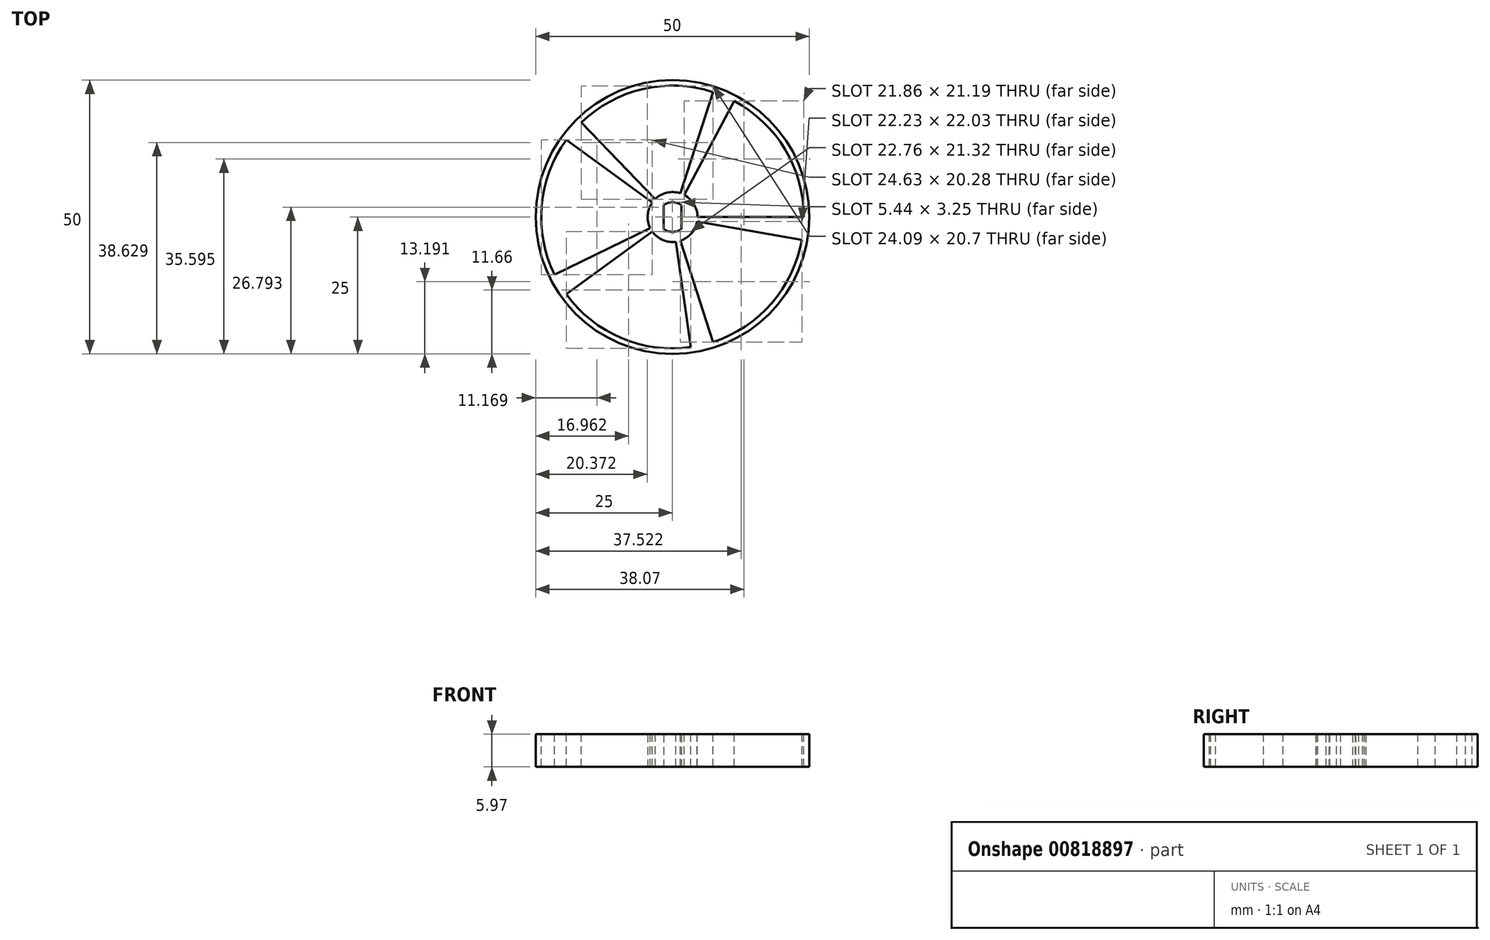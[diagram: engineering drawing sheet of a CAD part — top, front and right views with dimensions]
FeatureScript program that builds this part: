
annotation { "Feature Type Name" : "Feature", "Feature Type Description" : "" }
export const myFeature = defineFeature(function(context is Context, id is Id, definition is map)
    precondition{}
    {
        {
            var Q0;
            Q0=qCreatedBy(makeId("Top.planeOp"),FACE);
            var sketch = newSketch(context, id + "F0", { "sketchPlane" : qUnion([Q0])});
            skArc(sketch, "E0", {"start": v(2.6, 5.8) * mm, "mid": v(-6.35, 0) * mm, "end": v(2.6, -5.8) * mm});
            skLineSegment(sketch, "E1", {"start": v(2.6, 5.8) * mm, "end": v(15.56, 0) * mm});
            skLineSegment(sketch, "E2", {"start": v(15.56, 0) * mm, "end": v(2.6, -5.8) * mm});
            skCircle(sketch, "E3", {"center": v(0, 0) * mm, "radius": 4.56 * mm});
            skLineSegment(sketch, "E4.bottom", {"start": v(-1.63, 2.18) * mm, "end": v(1.63, 2.18) * mm, "construction": true});
            skLineSegment(sketch, "E4.top", {"start": v(-1.63, -2.18) * mm, "end": v(1.63, -2.18) * mm, "construction": true});
            skLineSegment(sketch, "E4.left", {"start": v(-1.63, 2.18) * mm, "end": v(-1.63, -2.18) * mm});
            skLineSegment(sketch, "E4.right", {"start": v(1.63, 2.18) * mm, "end": v(1.63, -2.18) * mm});
            skArc(sketch, "E5", {"start": v(1.63, 2.18) * mm, "mid": v(0, 2.72) * mm, "end": v(-1.63, 2.18) * mm});
            skArc(sketch, "E6", {"start": v(-1.63, -2.18) * mm, "mid": v(0, -2.72) * mm, "end": v(1.63, -2.18) * mm});
            skArc(sketch, "E7", {"start": v(5.5, -2.76) * mm, "mid": v(6.15, 0) * mm, "end": v(5.5, 2.76) * mm});
            skLineSegment(sketch, "E8", {"start": v(5.5, -2.76) * mm, "end": v(11.67, 0) * mm});
            skLineSegment(sketch, "E9", {"start": v(11.67, 0) * mm, "end": v(5.5, 2.76) * mm});
            skLineSegment(sketch, "E10", {"start": v(5.5, 2.76) * mm, "end": v(5.5, -2.76) * mm, "construction": true});
            skSolve(sketch);
        }
        {
            var Q0;
            Q0=makeQuery(id+"F0.imprint","IMPRINT",FACE,{"disambiguationData":[TD([[makeQuery(id+"F0.imprint","IMPRINT",EDGE,{"derivedFrom":sQuery(id+"F0.wireOp",EDGE,"E3")}),1.0]])]});
            extrude(context, id + "F1", {"entities" : qUnion([Q0]), "depth" : 5.97 * mm, "offsetDistance" : 25.4 * mm});
        }
        {
            var Q0;
            Q0=makeQuery(id+"F1.opExtrude","CAP_FACE",FACE,{"disambiguationData":[OSD([sQuery(id+"F0.wireOp",EDGE,"E3"),sQuery(id+"F0.wireOp",EDGE,"E4.left"),sQuery(id+"F0.wireOp",EDGE,"E4.right"),sQuery(id+"F0.wireOp",EDGE,"E5"),sQuery(id+"F0.wireOp",EDGE,"E6")])],"isStart":false});
            var sketch = newSketch(context, id + "F2", { "sketchPlane" : qUnion([Q0])});
            skCircle(sketch, "E11", {"center": v(0, 0) * mm, "radius": 25 * mm});
            skLineSegment(sketch, "E12", {"start": v(0, 0) * mm, "end": v(4.56, 0) * mm, "construction": true});
            skLineSegment(sketch, "E13", {"start": v(0, 0) * mm, "end": v(4.5, -0.8) * mm, "construction": true});
            skLineSegment(sketch, "E14", {"start": v(4.5, -0.8) * mm, "end": v(23.64, -4.17) * mm});
            skLineSegment(sketch, "E15", {"start": v(4.56, 0) * mm, "end": v(24, 0) * mm});
            skArc(sketch, "E16.0", {"start": v(4.5, -0.8) * mm, "mid": v(4.54, -0.4) * mm, "end": v(4.56, 0) * mm});
            skLineSegment(sketch, "E17.1.0", {"start": v(2.14, 4.03) * mm, "end": v(11.27, 21.2) * mm});
            skLineSegment(sketch, "E17.1.1", {"start": v(1.4, 4.34) * mm, "end": v(7.42, 22.83) * mm});
            skLineSegment(sketch, "E17.2.0", {"start": v(-3.17, 3.28) * mm, "end": v(-16.67, 17.26) * mm});
            skLineSegment(sketch, "E17.2.1", {"start": v(-3.69, 2.68) * mm, "end": v(-19.42, 14.1) * mm});
            skLineSegment(sketch, "E17.3.0", {"start": v(-4.1, -2) * mm, "end": v(-21.57, -10.52) * mm});
            skLineSegment(sketch, "E17.3.1", {"start": v(-3.69, -2.68) * mm, "end": v(-19.42, -14.1) * mm});
            skLineSegment(sketch, "E17.4.0", {"start": v(0.63, -4.51) * mm, "end": v(3.34, -23.77) * mm});
            skLineSegment(sketch, "E17.4.1", {"start": v(1.4, -4.34) * mm, "end": v(7.42, -22.83) * mm});
            skArc(sketch, "E18.trimOffspring", {"start": v(0.63, -4.51) * mm, "mid": v(1.03, -4.44) * mm, "end": v(1.4, -4.34) * mm});
            skArc(sketch, "E19.trimOffspring", {"start": v(-4.1, -2) * mm, "mid": v(-3.9, -2.35) * mm, "end": v(-3.69, -2.68) * mm});
            skArc(sketch, "E20.trimOffspring", {"start": v(-3.17, 3.28) * mm, "mid": v(-3.44, 3) * mm, "end": v(-3.69, 2.68) * mm});
            skArc(sketch, "E21.trimOffspring", {"start": v(2.14, 4.03) * mm, "mid": v(1.78, 4.2) * mm, "end": v(1.4, 4.34) * mm});
            skArc(sketch, "E22.0", {"start": v(24, 0) * mm, "mid": v(20.57, 12.36) * mm, "end": v(11.27, 21.2) * mm});
            skPoint(sketch, "E23.orphan", {"position": v(24.62, -4.34) * mm});
            skPoint(sketch, "E24.orphan", {"position": v(25, 0) * mm});
            skPoint(sketch, "E25.orphan", {"position": v(11.74, 22.07) * mm});
            skArc(sketch, "E26.trimOffspring", {"start": v(7.42, 22.83) * mm, "mid": v(-5.4, 23.38) * mm, "end": v(-16.67, 17.26) * mm});
            skPoint(sketch, "E27.orphan", {"position": v(7.73, 23.78) * mm});
            skArc(sketch, "E28.trimOffspring", {"start": v(-19.42, 14.1) * mm, "mid": v(-23.9, 2.1) * mm, "end": v(-21.57, -10.52) * mm});
            skPoint(sketch, "E29.orphan", {"position": v(-17.37, 17.98) * mm});
            skPoint(sketch, "E30.orphan", {"position": v(-20.23, 14.7) * mm});
            skArc(sketch, "E31.trimOffspring", {"start": v(-19.42, -14.1) * mm, "mid": v(-9.38, -22.1) * mm, "end": v(3.34, -23.77) * mm});
            skPoint(sketch, "E32.orphan", {"position": v(-20.23, -14.7) * mm});
            skPoint(sketch, "E33.orphan", {"position": v(-22.47, -10.96) * mm});
            skArc(sketch, "E34.trimOffspring", {"start": v(7.42, -22.83) * mm, "mid": v(18.11, -15.75) * mm, "end": v(23.64, -4.17) * mm});
            skPoint(sketch, "E35.orphan", {"position": v(3.48, -24.76) * mm});
            skPoint(sketch, "E36.orphan", {"position": v(7.73, -23.78) * mm});
            skSolve(sketch);
        }
        {
            var Q0;
            Q0 = qSketchRegion(id + "F2", true);
            var Q1;
            Q1=makeQuery(id+"F1.opExtrude","CAP_FACE",FACE,{"disambiguationData":[OSD([sQuery(id+"F0.wireOp",EDGE,"E3"),sQuery(id+"F0.wireOp",EDGE,"E4.left"),sQuery(id+"F0.wireOp",EDGE,"E4.right"),sQuery(id+"F0.wireOp",EDGE,"E5"),sQuery(id+"F0.wireOp",EDGE,"E6")])],"isStart":true});
            extrude(context, id + "F3", {"entities" : qUnion([Q0]), "operationType" : NewBodyOperationType.ADD, "endBound" : BoundingType.UP_TO_SURFACE, "oppositeDirection" : true, "depth" : 25.4 * mm, "endBoundEntityFace" : qUnion([Q1]), "offsetDistance" : 25.4 * mm});
        }
    });
